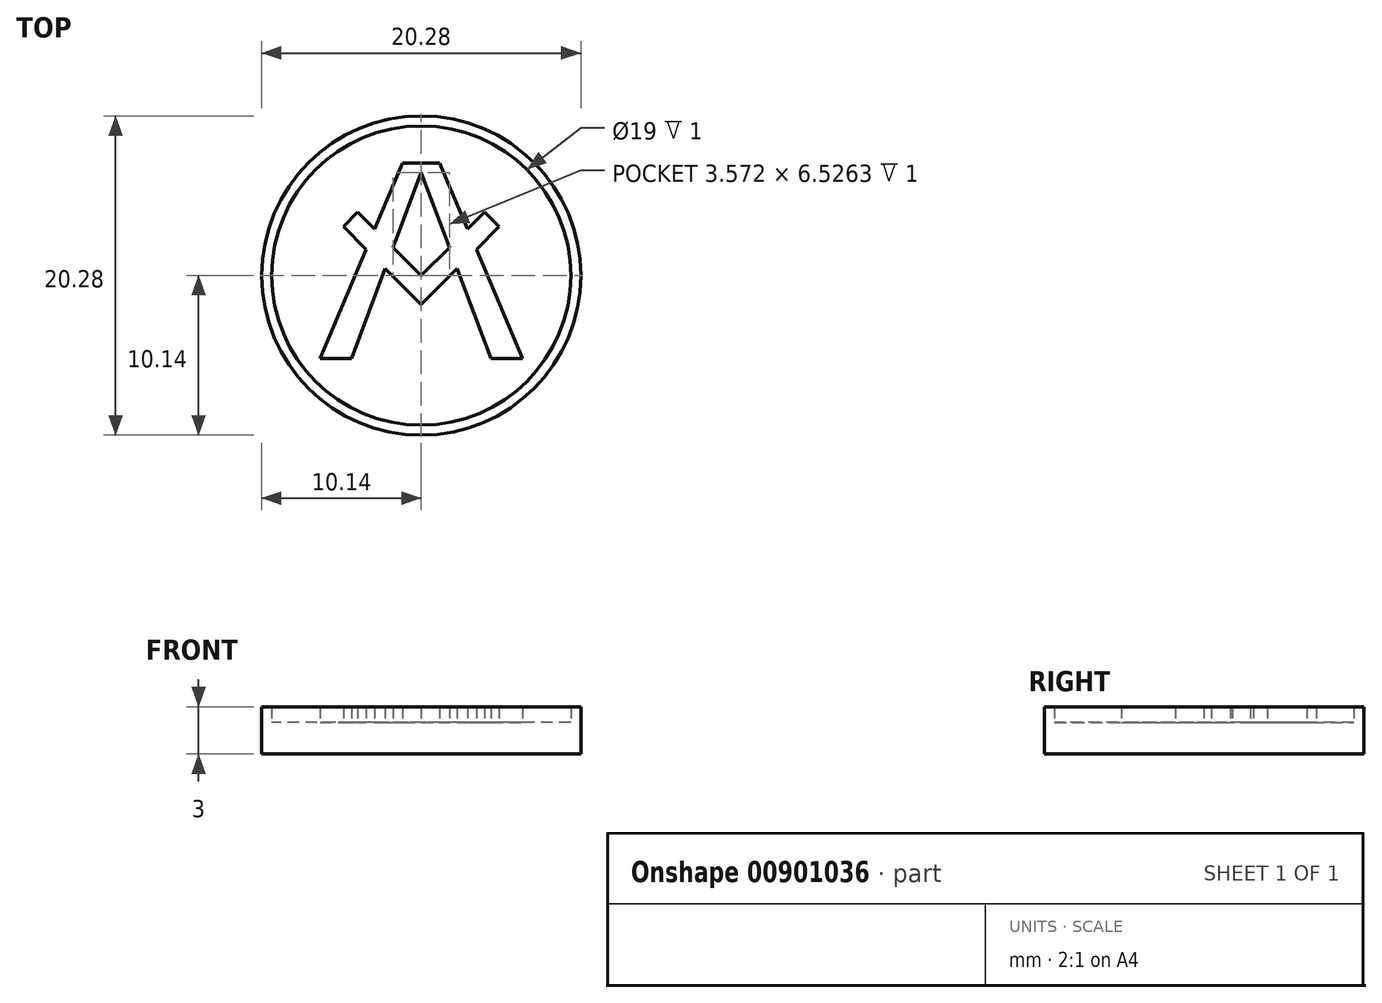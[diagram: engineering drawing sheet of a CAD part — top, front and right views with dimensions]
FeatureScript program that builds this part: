
annotation { "Feature Type Name" : "Feature", "Feature Type Description" : "" }
export const myFeature = defineFeature(function(context is Context, id is Id, definition is map)
    precondition{}
    {
        {
            var Q0;
            Q0=qCreatedBy(makeId("Top.planeOp"),FACE);
            var sketch = newSketch(context, id + "F0", { "sketchPlane" : qUnion([Q0])});
            skCircle(sketch, "E0", {"center": v(0, 0) * mm, "radius": 10.14 * mm});
            skSolve(sketch);
        }
        {
            var Q0;
            Q0=makeQuery(id+"F0.imprint","IMPRINT",FACE,{"disambiguationData":[TD([[makeQuery(id+"F0.imprint","IMPRINT",EDGE,{"derivedFrom":sQuery(id+"F0.wireOp",EDGE,"E0")}),1.0]])]});
            extrude(context, id + "F1", {"entities" : qUnion([Q0]), "oppositeDirection" : true, "depth" : 2 * mm, "offsetDistance" : 25 * mm});
        }
        {
            var Q0;
            Q0=makeQuery(id+"F1.opExtrude","CAP_FACE",FACE,{"disambiguationData":[OSD([sQuery(id+"F0.wireOp",EDGE,"E0")])],"isStart":true});
            var sketch = newSketch(context, id + "F2", { "sketchPlane" : qUnion([Q0])});
            skLineSegment(sketch, "E1", {"start": v(0, 0) * mm, "end": v(4.03, 4.03) * mm});
            skLineSegment(sketch, "E2", {"start": v(4.03, 4.03) * mm, "end": v(4.95, 3.12) * mm});
            skLineSegment(sketch, "E3", {"start": v(4.95, 3.12) * mm, "end": v(0, -1.83) * mm});
            skLineSegment(sketch, "E4", {"start": v(0, 6.53) * mm, "end": v(1.79, 1.79) * mm});
            skLineSegment(sketch, "E5", {"start": v(4.44, -5.26) * mm, "end": v(6.44, -5.26) * mm});
            skLineSegment(sketch, "E6", {"start": v(6.44, -5.26) * mm, "end": v(3.5, 1.67) * mm});
            skLineSegment(sketch, "E7", {"start": v(0, 0) * mm, "end": v(0, 0.78) * mm});
            skLineSegment(sketch, "E8.MirrorCS", {"start": v(-4.95, 3.12) * mm, "end": v(0, -1.83) * mm});
            skLineSegment(sketch, "E9.MirrorCS", {"start": v(-4.44, -5.26) * mm, "end": v(-6.44, -5.26) * mm});
            skLineSegment(sketch, "E10.MirrorCS", {"start": v(0, 0) * mm, "end": v(-4.03, 4.03) * mm});
            skLineSegment(sketch, "E11.MirrorCS", {"start": v(-6.44, -5.26) * mm, "end": v(-3.5, 1.67) * mm});
            skLineSegment(sketch, "E12.MirrorCS", {"start": v(-4.03, 4.03) * mm, "end": v(-4.95, 3.12) * mm});
            skLineSegment(sketch, "E13.MirrorCS", {"start": v(0, 6.53) * mm, "end": v(-1.79, 1.79) * mm});
            skLineSegment(sketch, "E14", {"start": v(-1.17, 7.14) * mm, "end": v(1.17, 7.14) * mm});
            skLineSegment(sketch, "E15.trimOffspring", {"start": v(2.95, 2.95) * mm, "end": v(1.17, 7.14) * mm});
            skLineSegment(sketch, "E16.trimOffspring", {"start": v(2.29, 0.46) * mm, "end": v(4.44, -5.26) * mm});
            skLineSegment(sketch, "E17.trimOffspring", {"start": v(-2.29, 0.46) * mm, "end": v(-4.44, -5.26) * mm});
            skLineSegment(sketch, "E18.trimOffspring", {"start": v(-2.95, 2.95) * mm, "end": v(-1.17, 7.14) * mm});
            skSolve(sketch);
        }
        {
            var Q0;
            Q0=makeQuery(id+"F2.imprint","IMPRINT",FACE,{"disambiguationData":[TD([[makeQuery(id+"F2.imprint","IMPRINT",EDGE,{"derivedFrom":sQuery(id+"F2.wireOp",EDGE,"E5")}),1.0]])]});
            var Q1;
            {var subQ3=sQuery(id+"F2.wireOp",EDGE,"E4");Q1=makeQuery(id+"F2.imprint","IMPRINT",FACE,{"disambiguationData":[TD([[makeQuery(id+"F2.imprint","IMPRINT",EDGE,{"derivedFrom":subQ3}),1.0]])]});}
            var Q2;
            Q2=makeQuery(id+"F2.imprint","IMPRINT",FACE,{"disambiguationData":[TD([[makeQuery(id+"F2.imprint","IMPRINT",EDGE,{"derivedFrom":sQuery(id+"F2.wireOp",EDGE,"E9.MirrorCS")}),-1.0]])]});
            var Q3;
            {var subQ7=sQuery(id+"F2.wireOp",EDGE,"E2");Q3=makeQuery(id+"F2.imprint","IMPRINT",FACE,{"disambiguationData":[TD([[makeQuery(id+"F2.imprint","IMPRINT",EDGE,{"derivedFrom":subQ7}),-1.0]])]});}
            extrude(context, id + "F3", {"entities" : qUnion([Q0, Q1, Q2, Q3]), "operationType" : NewBodyOperationType.ADD, "depth" : 1 * mm, "offsetDistance" : 25 * mm});
        }
        {
            var Q0;
            {var subQ8=sQuery(id+"F0.wireOp",EDGE,"E0");Q0=makeQuery(id+"F3.boolean.opBoolean","SPLIT",FACE,{"disambiguationData":[TD([makeQuery(id+"F1.opExtrude","SWEPT_FACE",FACE,{"disambiguationData":[OSD([subQ8])]})])],"derivedFrom":makeQuery(id+"F1.opExtrude","CAP_FACE",FACE,{"disambiguationData":[OSD([subQ8])],"isStart":true})});}
            var sketch = newSketch(context, id + "F4", { "sketchPlane" : qUnion([Q0])});
            skCircle(sketch, "E19", {"center": v(0, 0) * mm, "radius": 10.14 * mm});
            skCircle(sketch, "E20", {"center": v(0, 0) * mm, "radius": 9.5 * mm});
            skSolve(sketch);
        }
        {
            var Q0;
            Q0=makeQuery(id+"F4.imprint","IMPRINT",FACE,{"disambiguationData":[TD([[makeQuery(id+"F4.imprint","IMPRINT",EDGE,{"derivedFrom":sQuery(id+"F4.wireOp",EDGE,"E19")}),1.0]])]});
            extrude(context, id + "F5", {"entities" : qUnion([Q0]), "operationType" : NewBodyOperationType.ADD, "depth" : 1 * mm, "offsetDistance" : 25 * mm});
        }
    });
